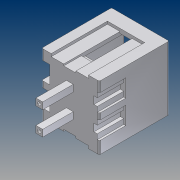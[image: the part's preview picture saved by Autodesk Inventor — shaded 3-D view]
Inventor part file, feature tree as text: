
AUTODESK INVENTOR PART (.ipt)
format: ipt  version: unknown  size: 309,248 bytes
history: native  units: mm (DEFAULTED — no unit token found)
features: sketch x16, extrude x15, pattern_linear x4, projected_geometry x2, other x1
ambient origin geometry x8: Origin, YZ Plane, XZ Plane, XY Plane, X Axis, Y Axis, Z Axis, Center Point
feature tree (38):
  extrude  "Extrusion1"  Depth=7.5mm TaperAngle=0.0deg
  extrude  "Extrusion2"  Depth=7.7mm TaperAngle=0.0deg
  extrude  "Extrusion3"  Depth=6.0mm TaperAngle=0.0deg
  extrude  "Extrusion4"  Depth=20.0mm TaperAngle=0.0deg
  extrude  "Extrusion5"  Depth=20.0mm TaperAngle=0.0deg
  extrude  "Extrusion6"  Depth=20.0mm TaperAngle=0.0deg
  extrude  "Extrusion7"  Depth=8.3mm TaperAngle=0.0deg
  pattern_linear  "Rectangular Pattern1"  Count1=2 Spacing1=3.5mm
  extrude  "Extrusion8"  Depth=3.9mm TaperAngle=0.0deg
  pattern_linear  "Rectangular Pattern2"  [2 undecoded]
  extrude  "Extrusion9"  [1 undecoded]
  pattern_linear  "Rectangular Pattern3"  [2 undecoded]
  extrude  "Extrusion10"  [1 undecoded]
  extrude  "Extrusion11"  [1 undecoded]
  extrude  "Extrusion12"  [1 undecoded]
  pattern_linear  "Rectangular Pattern4"  [2 undecoded]
  extrude  "Extrusion13"  [1 undecoded]
  extrude  "Extrusion14"  [1 undecoded]
  sketch  "Sketch15"
  other  "Work Axis1"
  extrude  "Extrusion15"  [1 undecoded]
  sketch  "Skizze_1"  dims[d0=9.4mm d1=0.0mm d2=7.5mm d3=0.0mm]
  sketch  "Skizze_2"  dims[d4=7.7mm d5=0.0mm d6=7.7mm d7=0.0mm]
  sketch  "Skizze_3"  dims[d8=6.0mm d9=0.0mm d10=6.0mm d11=0.0mm]
  sketch  "Skizze_4"  dims[d12=3.6mm d13=0.0mm d14=20.0mm d16=3.5mm d17=10.0mm d19=0.0mm]
  sketch  "Skizze_5"  dims[d20=9.3mm d21=0.0mm d22=20.0mm d24=3.5mm d25=10.0mm d27=0.0mm]
  sketch  "Skizze_6"  dims[d28=4.5mm d29=0.0mm d30=20.0mm d32=3.5mm d33=10.0mm d35=0.0mm]
  sketch  "Skizze_7"  dims[d36=8.3mm d37=0.0mm d38=8.3mm d39=0.0mm]
  sketch  "Skizze_9"  dims[d40=9.15mm d41=0.0mm d42=20.0mm d44=3.5mm d45=10.0mm d47=0.0mm]
  sketch  "Skizze_11"  dims[d48=3.9mm d49=0.0mm d50=3.9mm d51=0.0mm]
  sketch  "Skizze_13"  dims[d52=0.5mm]
  sketch  "Skizze_14"  dims[d53=10.0mm d54=0.0mm]
  sketch  "Skizze_15"
  sketch  "Skizze_17"
  sketch  "Skizze_18"
  sketch  "Sketch16"
  projected_geometry  "Projected Loop1"
  projected_geometry  "Projected Loop2"
note: 13 required parameter values undecoded (feature->parameter linkage not recoverable at this tier; creation-order binding heuristic only, values carry confidence <= 0.55)
